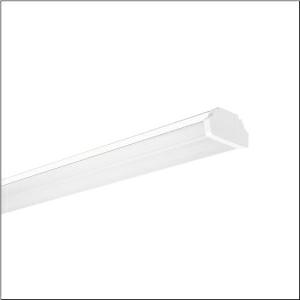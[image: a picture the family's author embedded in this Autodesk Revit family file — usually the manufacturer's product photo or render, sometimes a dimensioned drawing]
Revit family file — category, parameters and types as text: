
# Revit family: modario_31_gen_2_53bm812cv6c5d2_1f90
name_source: partatom
category: Lighting Fixtures
units: mm (PartAtom-declared; Revit-internal decimal feet)

## family parameters
Cut with Voids When Loaded = No
Host = Face
Light Source = No
Part Type = Normal
Room Calculation Point = No
Round Connector Dimension = Use Diameter
Shared = No

## types (1)
- --- (1 x LED, 12660 lm, 68.5 W, 6500K)
    Apparent Load = 69 VA
    CIE Flux Codes = 47 80 95 93 100
    Color Rendering = 80
    Color Temperature = 6500K
    Default Elevation = 1800 mm
    Description = Modario 31 Gen.2, luminaire insert, of sheet steel, coil coated, white, length: 1.495mm, width: 81mm, height: 82mm, 5x system unit, system units: 299mm, LED rated luminous flux: 12.660lm, light colour: 865, SDCM (Standard Deviation of Colour Matching)MacAdam ≤ 3 SDCM (initial), control gear: ON/OFF Multilumen, CLOi, with plug, 3-pole, with phase selection, mains connection: 220..240V, AC, 50/60Hz, start of lifetime: 69W, end of service life: 82W, through-wiring accessed according to module size, primary optical cover: cover, of PMMA, light emission: direct distribution, primary light characteristic: symmetric, protection rating (complete): IP20, protection rating (LED compartment): IP50, insulation class (complete): insulation class I (protective earthing), certification: CE, ENEC, VDE, UKCA, impact resistance: IK03, permissible ambient temperature for indoor applications: -35..+35°C, corresponds to IFS (International Featured Standards) requirements for safety and quality in the food industry, reducing of maximum allowable ambient temperature of 5°C with ceiling mounting, IP40 when using the optional accessory 5TP9018, packaging unit: 1 piece
    Height = 92 mm
    Lamp = 1 x LED
    Lamp Light Flux = 12660 lm
    Lamp Power = 68.5 W
    Lamp count = 1
    Length = 1495 mm
    Luminous efficacy = 185 lm/W
    Manufacturer = Siteco
    ModVariant = No
    Model = 53BM812CV6C5D2
    Mounting Place = Ceiling
    Mounting Type = Pendant
    Number of Poles = 1
    OnlyDefault = Yes
    Power Factor = 1
    Product Name = Modario 31 Gen.2
    Product group = luminaire insert | ceiling pendant
    ProductGroupID = 901
    Protection Class = Protection class I
    Protection Degree = IP 20
    RLX_Detail_Level = 1
    RLX_Emergency_Light_Flux = 0 lm
    RLX_Emergency_Type = 0
    RLX_Emergency_Type_DB = No
    RlxData = <blob elided: 39961 chars, md5=0beb600e>
    Socket = socket
    Standby Power = 0 W
    System Light Flux = 12660 lm
    System Power = 69 W
    Type Comments = factory setting: luminous flux: 100 % | (A | C | E) | 161 mA
    Type Image = l_1341886.jpg
    URL = http://relux.com
    VarID = @adj_052299
    Voltage = 0 V
    Weight = 0.00 kg
    Width = 81 mm

## geometry (parser evidence)
native form markers: Blend x4, Sweep x11
no freeform markers — native parametric forms only
